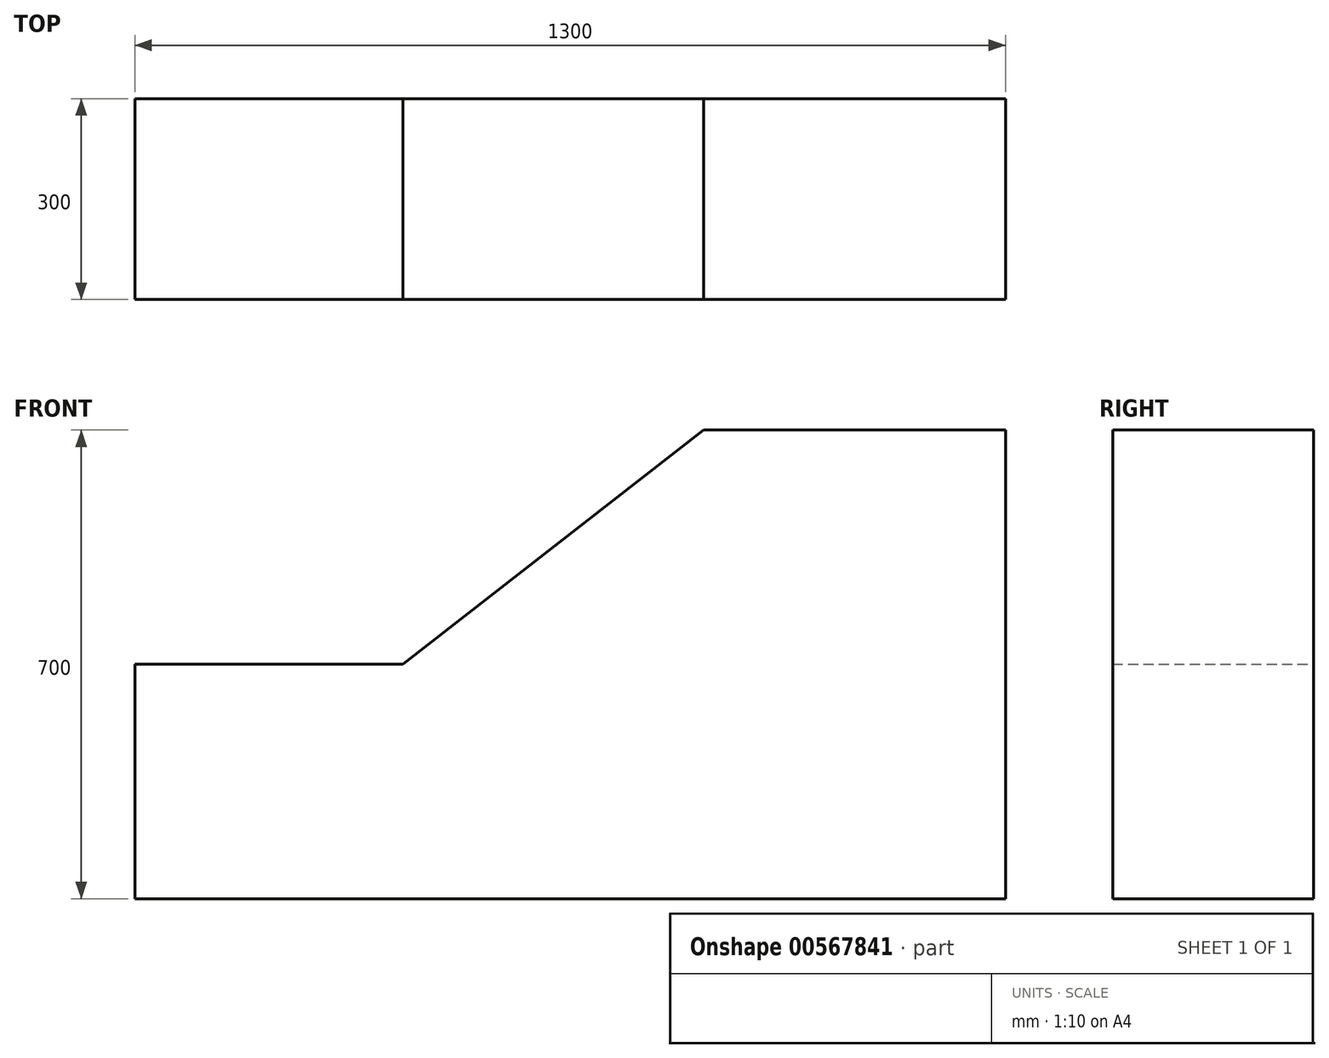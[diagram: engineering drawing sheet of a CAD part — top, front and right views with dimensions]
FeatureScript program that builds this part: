
annotation { "Feature Type Name" : "Feature", "Feature Type Description" : "" }
export const myFeature = defineFeature(function(context is Context, id is Id, definition is map)
    precondition{}
    {
        {
            var Q0;
            Q0=qCreatedBy(makeId("Front.planeOp"),FACE);
            var sketch = newSketch(context, id + "F0", { "sketchPlane" : qUnion([Q0])});
            skLineSegment(sketch, "E0.bottom", {"start": v(-650, -350) * mm, "end": v(650, -350) * mm});
            skLineSegment(sketch, "E0.top", {"start": v(-650, 350) * mm, "end": v(650, 350) * mm});
            skLineSegment(sketch, "E0.left", {"start": v(-650, -350) * mm, "end": v(-650, 350) * mm});
            skLineSegment(sketch, "E0.right", {"start": v(650, -350) * mm, "end": v(650, 350) * mm});
            skPoint(sketch, "E0.middle", {"position": v(0, 0) * mm});
            skLineSegment(sketch, "E1", {"start": v(199.14, 350) * mm, "end": v(-250, 0) * mm});
            skLineSegment(sketch, "E2", {"start": v(-250, 0) * mm, "end": v(-650, 0) * mm});
            skLineSegment(sketch, "E3", {"start": v(-650, 0) * mm, "end": v(-250, 0) * mm});
            skSolve(sketch);
        }
        {
            var Q0;
            {var subQ1=sQuery(id+"F0.wireOp",EDGE,"E0.bottom");Q0=makeQuery(id+"F0.imprint","IMPRINT",FACE,{"disambiguationData":[TD([[makeQuery(id+"F0.imprint","IMPRINT",EDGE,{"derivedFrom":subQ1}),1.0]])]});}
            extrude(context, id + "F1", {"entities" : qUnion([Q0]), "depth" : 300 * mm, "offsetDistance" : 25.4 * mm});
        }
    });
